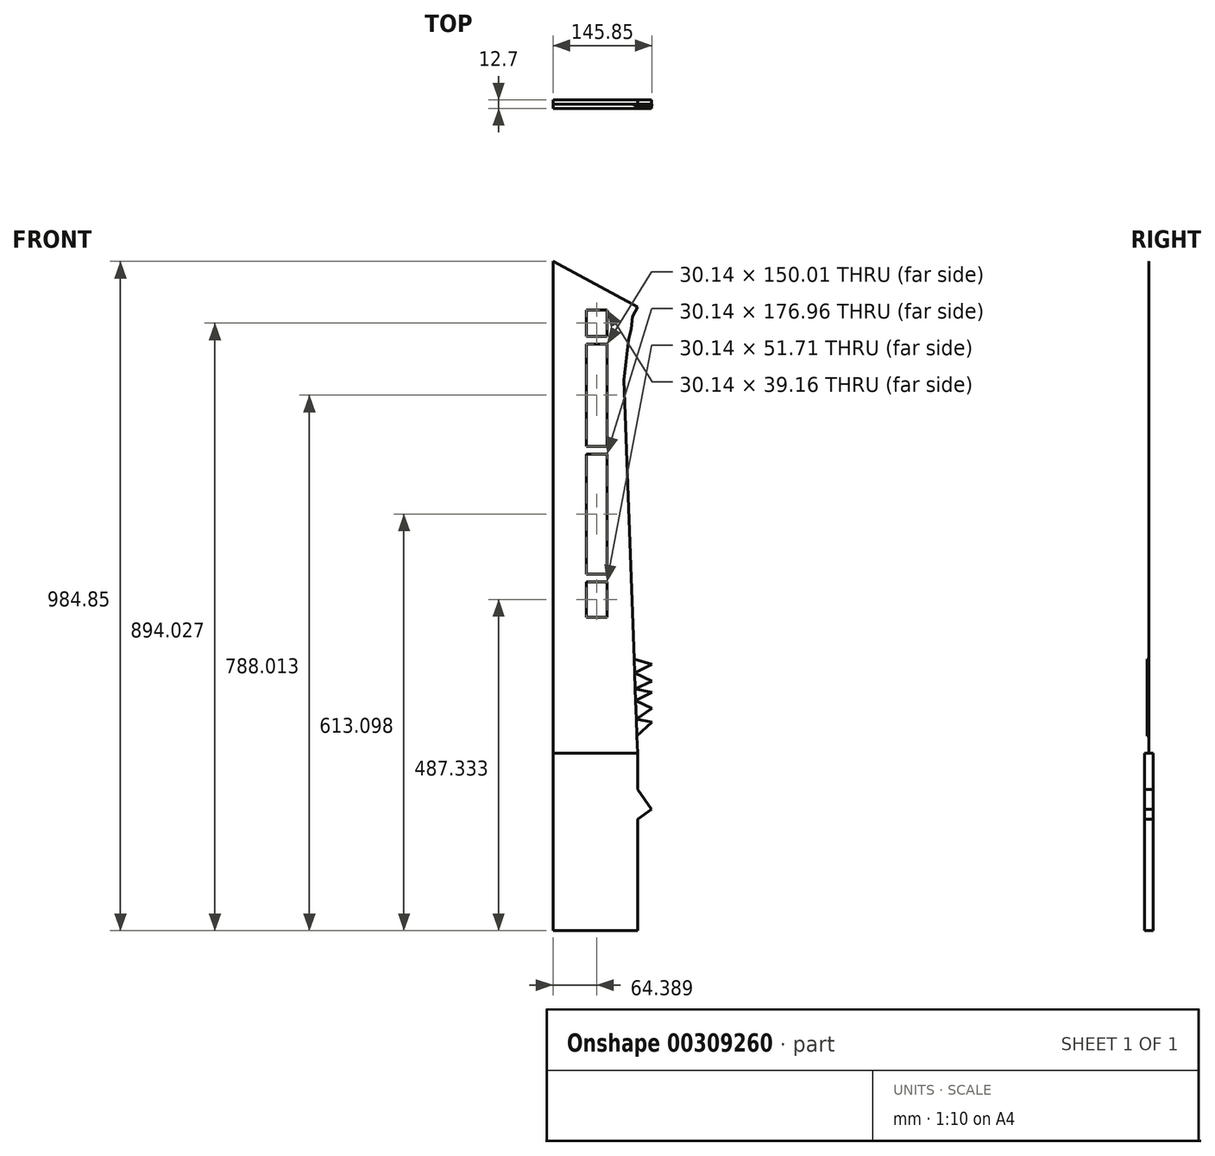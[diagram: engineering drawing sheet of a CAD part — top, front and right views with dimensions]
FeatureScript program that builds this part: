
annotation { "Feature Type Name" : "Feature", "Feature Type Description" : "" }
export const myFeature = defineFeature(function(context is Context, id is Id, definition is map)
    precondition{}
    {
        {
            var Q0;
            Q0=qCreatedBy(makeId("Front.planeOp"),FACE);
            var sketch = newSketch(context, id + "F0", { "sketchPlane" : qUnion([Q0])});
            skLineSegment(sketch, "E0", {"start": v(-62.14, 310.68) * mm, "end": v(-62.14, -141.45) * mm});
            skLineSegment(sketch, "E1", {"start": v(-32, -141.45) * mm, "end": v(-32, 310.68) * mm});
            skLineSegment(sketch, "E2", {"start": v(-62.14, 310.68) * mm, "end": v(-32, 310.68) * mm});
            skLineSegment(sketch, "E3", {"start": v(-62.14, -141.45) * mm, "end": v(-32, -141.45) * mm});
            skLineSegment(sketch, "E4", {"start": v(-111.46, 381.92) * mm, "end": v(-111.46, -341.64) * mm});
            skLineSegment(sketch, "E5", {"start": v(-111.46, -341.64) * mm, "end": v(12.94, -341.64) * mm});
            skLineSegment(sketch, "E6", {"start": v(12.94, 314.91) * mm, "end": v(-111.46, 381.92) * mm});
            skLineSegment(sketch, "E7", {"start": v(-62.14, -78.31) * mm, "end": v(-32, -78.31) * mm});
            skLineSegment(sketch, "E8", {"start": v(-62.14, -89.74) * mm, "end": v(-32, -89.74) * mm});
            skLineSegment(sketch, "E9", {"start": v(-62.14, 98.65) * mm, "end": v(-32, 98.65) * mm});
            skLineSegment(sketch, "E10", {"start": v(-62.14, 110.08) * mm, "end": v(-32, 110.08) * mm});
            skLineSegment(sketch, "E11", {"start": v(-62.14, 271.52) * mm, "end": v(-32, 271.52) * mm});
            skLineSegment(sketch, "E12", {"start": v(-62.14, 260.09) * mm, "end": v(-32, 260.09) * mm});
            skLineSegment(sketch, "E13", {"start": v(12.94, 314.91) * mm, "end": v(8.97, 307.55) * mm});
            skLineSegment(sketch, "E14", {"start": v(8.97, 307.55) * mm, "end": v(5.4, 300.9) * mm});
            skLineSegment(sketch, "E15", {"start": v(5.4, 300.9) * mm, "end": v(3.83, 282.65) * mm});
            skLineSegment(sketch, "E16", {"start": v(3.83, 282.65) * mm, "end": v(0, 267.31) * mm});
            skLineSegment(sketch, "E17", {"start": v(0, 267.31) * mm, "end": v(-6.84, 207.65) * mm});
            skLineSegment(sketch, "E18", {"start": v(-6.84, 207.65) * mm, "end": v(12.94, -341.64) * mm});
            skSolve(sketch);
        }
        {
            var Q0;
            Q0=makeQuery(id+"F0.imprint","IMPRINT",FACE,{"disambiguationData":[TD([[makeQuery(id+"F0.imprint","IMPRINT",EDGE,{"derivedFrom":sQuery(id+"F0.wireOp",EDGE,"E0")}),-1.0]])]});
            var Q1;
            {var subQ0=sQuery(id+"F0.wireOp",EDGE,"E9");Q1=makeQuery(id+"F0.imprint","IMPRINT",FACE,{"disambiguationData":[TD([[makeQuery(id+"F0.imprint","IMPRINT",EDGE,{"derivedFrom":subQ0}),1.0]])]});}
            var Q2;
            {var subQ0=sQuery(id+"F0.wireOp",EDGE,"E11");Q2=makeQuery(id+"F0.imprint","IMPRINT",FACE,{"disambiguationData":[TD([[makeQuery(id+"F0.imprint","IMPRINT",EDGE,{"derivedFrom":subQ0}),-1.0]])]});}
            var Q3;
            {var subQ0=sQuery(id+"F0.wireOp",EDGE,"E7");Q3=makeQuery(id+"F0.imprint","IMPRINT",FACE,{"disambiguationData":[TD([[makeQuery(id+"F0.imprint","IMPRINT",EDGE,{"derivedFrom":subQ0}),-1.0]])]});}
            extrude(context, id + "F1", {"entities" : qUnion([Q0, Q1, Q2, Q3]), "depth" : 0.25 * mm});
        }
        {
            var Q0;
            Q0=makeQuery(id+"F1.opExtrude","CAP_FACE",FACE,{"disambiguationData":[OSD([sQuery(id+"F0.wireOp",EDGE,"E0"),sQuery(id+"F0.wireOp",EDGE,"E1"),sQuery(id+"F0.wireOp",EDGE,"E2"),sQuery(id+"F0.wireOp",EDGE,"E3"),sQuery(id+"F0.wireOp",EDGE,"E4"),sQuery(id+"F0.wireOp",EDGE,"m02dCb16-lm57-EGja-fgRB-fwLYrAywwRAF"),sQuery(id+"F0.wireOp",EDGE,"E5"),sQuery(id+"F0.wireOp",EDGE,"E6")])],"isStart":false});
            var sketch = newSketch(context, id + "F2", { "sketchPlane" : qUnion([Q0])});
            skLineSegment(sketch, "E19", {"start": v(-111.46, -341.64) * mm, "end": v(-111.46, -602.93) * mm});
            skLineSegment(sketch, "E20", {"start": v(12.94, -341.64) * mm, "end": v(12.94, -395) * mm});
            skLineSegment(sketch, "E21", {"start": v(12.94, -395) * mm, "end": v(33.8, -424.18) * mm});
            skLineSegment(sketch, "E22", {"start": v(33.8, -424.18) * mm, "end": v(12.94, -439.08) * mm});
            skLineSegment(sketch, "E23", {"start": v(12.94, -439.08) * mm, "end": v(12.94, -602.93) * mm});
            skLineSegment(sketch, "E24", {"start": v(12.94, -602.93) * mm, "end": v(-111.46, -602.93) * mm});
            skLineSegment(sketch, "E25", {"start": v(-111.46, -602.93) * mm, "end": v(-111.46, -636.85) * mm});
            skLineSegment(sketch, "E26", {"start": v(-111.46, -636.85) * mm, "end": v(13.99, -636.85) * mm});
            skLineSegment(sketch, "E27", {"start": v(12.94, -602.93) * mm, "end": v(13.99, -636.85) * mm});
            skSolve(sketch);
        }
        {
            var Q0;
            Q0=makeQuery(id+"F2.imprint","IMPRINT",FACE,{"disambiguationData":[TD([[makeQuery(id+"F2.imprint","IMPRINT",EDGE,{"derivedFrom":sQuery(id+"F2.wireOp",EDGE,"E19")}),1.0]])]});
            extrude(context, id + "F3", {"entities" : qUnion([Q0]), "operationType" : NewBodyOperationType.ADD, "endBound" : BoundingType.SYMMETRIC, "depth" : 12.7 * mm});
        }
        {
            var Q0;
            Q0=makeQuery(id+"F1.opExtrude","CAP_FACE",FACE,{"disambiguationData":[OSD([sQuery(id+"F0.wireOp",EDGE,"E0"),sQuery(id+"F0.wireOp",EDGE,"E1"),sQuery(id+"F0.wireOp",EDGE,"E2"),sQuery(id+"F0.wireOp",EDGE,"E3"),sQuery(id+"F0.wireOp",EDGE,"E4"),sQuery(id+"F0.wireOp",EDGE,"E5"),sQuery(id+"F0.wireOp",EDGE,"E6"),sQuery(id+"F0.wireOp",EDGE,"E7"),sQuery(id+"F0.wireOp",EDGE,"E8"),sQuery(id+"F0.wireOp",EDGE,"E9"),sQuery(id+"F0.wireOp",EDGE,"E10"),sQuery(id+"F0.wireOp",EDGE,"E11"),sQuery(id+"F0.wireOp",EDGE,"E12"),sQuery(id+"F0.wireOp",EDGE,"E13"),sQuery(id+"F0.wireOp",EDGE,"E14"),sQuery(id+"F0.wireOp",EDGE,"E15"),sQuery(id+"F0.wireOp",EDGE,"E16"),sQuery(id+"F0.wireOp",EDGE,"E17"),sQuery(id+"F0.wireOp",EDGE,"E18")])],"isStart":false});
            var sketch = newSketch(context, id + "F4", { "sketchPlane" : qUnion([Q0])});
            skLineSegment(sketch, "E28", {"start": v(7.96, -203.27) * mm, "end": v(34.4, -210.73) * mm});
            skLineSegment(sketch, "E29", {"start": v(34.4, -210.73) * mm, "end": v(8.68, -223.44) * mm});
            skLineSegment(sketch, "E30", {"start": v(8.68, -223.44) * mm, "end": v(34.4, -235.65) * mm});
            skLineSegment(sketch, "E31", {"start": v(34.4, -235.65) * mm, "end": v(9.53, -247.01) * mm});
            skLineSegment(sketch, "E32", {"start": v(9.53, -247.01) * mm, "end": v(34.4, -252.22) * mm});
            skLineSegment(sketch, "E33", {"start": v(34.4, -252.22) * mm, "end": v(10.16, -264.44) * mm});
            skLineSegment(sketch, "E34", {"start": v(10.16, -264.44) * mm, "end": v(34.4, -275.45) * mm});
            skLineSegment(sketch, "E35", {"start": v(34.4, -275.45) * mm, "end": v(11.14, -291.8) * mm});
            skLineSegment(sketch, "E36", {"start": v(11.14, -291.8) * mm, "end": v(34.4, -295.8) * mm});
            skLineSegment(sketch, "E37", {"start": v(34.4, -295.8) * mm, "end": v(12.02, -316.26) * mm});
            skLineSegment(sketch, "E38", {"start": v(12.02, -316.26) * mm, "end": v(34.4, -327.97) * mm});
            skLineSegment(sketch, "E39", {"start": v(34.4, -327.97) * mm, "end": v(12.94, -341.64) * mm});
            skSolve(sketch);
        }
        {
            var Q0;
            {var subQ0=sQuery(id+"F4.wireOp",EDGE,"E28");Q0=makeQuery(id+"F4.imprint","IMPRINT",FACE,{"disambiguationData":[TD([[makeQuery(id+"F4.imprint","IMPRINT",EDGE,{"derivedFrom":subQ0}),-1.0]])]});}
            var Q1;
            {var subQ0=sQuery(id+"F4.wireOp",EDGE,"E30");Q1=makeQuery(id+"F4.imprint","IMPRINT",FACE,{"disambiguationData":[TD([[makeQuery(id+"F4.imprint","IMPRINT",EDGE,{"derivedFrom":subQ0}),-1.0]])]});}
            var Q2;
            {var subQ0=sQuery(id+"F4.wireOp",EDGE,"E32");Q2=makeQuery(id+"F4.imprint","IMPRINT",FACE,{"disambiguationData":[TD([[makeQuery(id+"F4.imprint","IMPRINT",EDGE,{"derivedFrom":subQ0}),-1.0]])]});}
            var Q3;
            {var subQ0=sQuery(id+"F4.wireOp",EDGE,"E34");Q3=makeQuery(id+"F4.imprint","IMPRINT",FACE,{"disambiguationData":[TD([[makeQuery(id+"F4.imprint","IMPRINT",EDGE,{"derivedFrom":subQ0}),-1.0]])]});}
            var Q4;
            {var subQ0=sQuery(id+"F4.wireOp",EDGE,"E36");Q4=makeQuery(id+"F4.imprint","IMPRINT",FACE,{"disambiguationData":[TD([[makeQuery(id+"F4.imprint","IMPRINT",EDGE,{"derivedFrom":subQ0}),-1.0]])]});}
            extrude(context, id + "F5", {"entities" : qUnion([Q0, Q1, Q2, Q3, Q4]), "depth" : 2.54 * mm});
        }
    });
